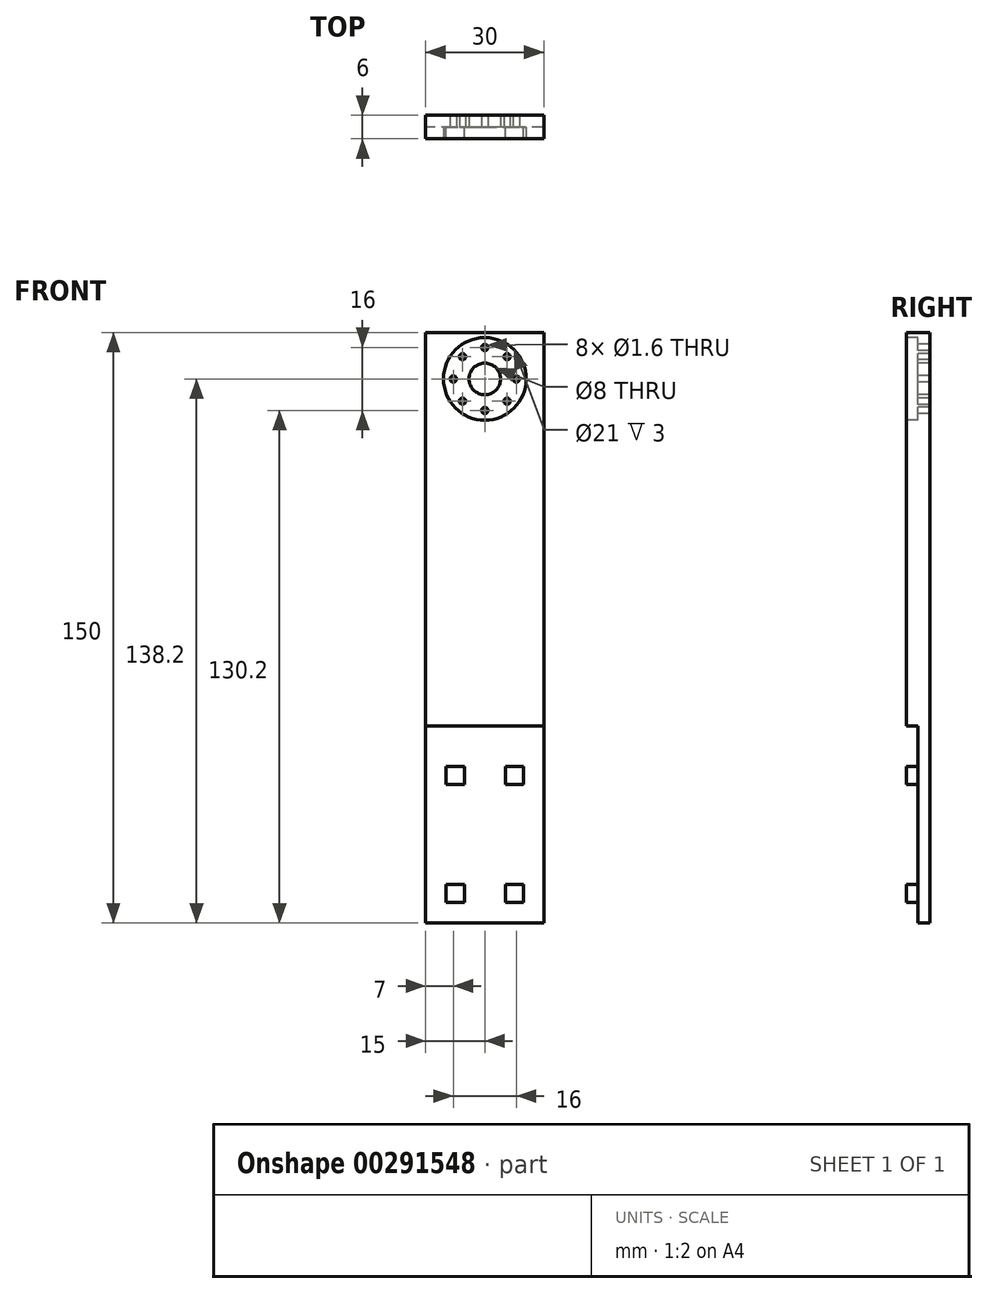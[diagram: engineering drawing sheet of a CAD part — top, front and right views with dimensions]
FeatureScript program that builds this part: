
annotation { "Feature Type Name" : "Feature", "Feature Type Description" : "" }
export const myFeature = defineFeature(function(context is Context, id is Id, definition is map)
    precondition{}
    {
        {
            var Q0;
            Q0=qCreatedBy(makeId("Top.planeOp"),FACE);
            var sketch = newSketch(context, id + "F0", { "sketchPlane" : qUnion([Q0])});
            skLineSegment(sketch, "E0.bottom", {"start": v(-15, 3) * mm, "end": v(15, 3) * mm});
            skLineSegment(sketch, "E0.top", {"start": v(-15, -3) * mm, "end": v(15, -3) * mm});
            skLineSegment(sketch, "E0.left", {"start": v(-15, 3) * mm, "end": v(-15, -3) * mm});
            skLineSegment(sketch, "E0.right", {"start": v(15, 3) * mm, "end": v(15, -3) * mm});
            skSolve(sketch);
        }
        {
            var Q0;
            Q0=qSketchRegion(id+"F0",true);
            extrude(context, id + "F1", {"entities" : qUnion([Q0]), "depth" : 150 * mm, "offsetDistance" : 25 * mm});
        }
        {
            var Q0;
            Q0=makeQuery(id+"F1.opExtrude","SWEPT_FACE",FACE,{"disambiguationData":[OSD([sQuery(id+"F0.wireOp",EDGE,"E0.top")])]});
            var sketch = newSketch(context, id + "F2", { "sketchPlane" : qUnion([Q0])});
            skCircle(sketch, "E1", {"center": v(0, 146.2) * mm, "radius": 0.8 * mm});
            skCircle(sketch, "E2", {"center": v(0, 138.2) * mm, "radius": 4 * mm});
            skCircle(sketch, "E3.1.0", {"center": v(-5.66, 143.86) * mm, "radius": 0.8 * mm});
            skCircle(sketch, "E3.2.0", {"center": v(-8, 138.2) * mm, "radius": 0.8 * mm});
            skCircle(sketch, "E3.3.0", {"center": v(-5.66, 132.54) * mm, "radius": 0.8 * mm});
            skCircle(sketch, "E3.4.0", {"center": v(0, 130.2) * mm, "radius": 0.8 * mm});
            skCircle(sketch, "E3.5.0", {"center": v(5.66, 132.54) * mm, "radius": 0.8 * mm});
            skCircle(sketch, "E3.6.0", {"center": v(8, 138.2) * mm, "radius": 0.8 * mm});
            skCircle(sketch, "E3.7.0", {"center": v(5.66, 143.86) * mm, "radius": 0.8 * mm});
            skSolve(sketch);
        }
        {
            var Q0;
            Q0=qSketchRegion(id+"F2",true);
            extrude(context, id + "F3", {"entities" : qUnion([Q0]), "operationType" : NewBodyOperationType.REMOVE, "endBound" : BoundingType.UP_TO_NEXT, "oppositeDirection" : true, "depth" : 25 * mm});
        }
        {
            var Q0;
            Q0=makeQuery(id+"F1.opExtrude","SWEPT_FACE",FACE,{"disambiguationData":[OSD([sQuery(id+"F0.wireOp",EDGE,"E0.left")])]});
            var sketch = newSketch(context, id + "F4", { "sketchPlane" : qUnion([Q0])});
            skLineSegment(sketch, "E4.bottom", {"start": v(0, 50) * mm, "end": v(3, 50) * mm});
            skLineSegment(sketch, "E4.top", {"start": v(0, 0) * mm, "end": v(3, 0) * mm});
            skLineSegment(sketch, "E4.left", {"start": v(0, 50) * mm, "end": v(0, 0) * mm});
            skLineSegment(sketch, "E4.right", {"start": v(3, 50) * mm, "end": v(3, 0) * mm});
            skSolve(sketch);
        }
        {
            var Q0;
            Q0=makeQuery(id+"F4.imprint","IMPRINT",FACE,{"disambiguationData":[TD([[makeQuery(id+"F4.imprint","IMPRINT",EDGE,{"derivedFrom":sQuery(id+"F4.wireOp",EDGE,"E4.bottom")}),-1.0]])]});
            extrude(context, id + "F5", {"entities" : qUnion([Q0]), "operationType" : NewBodyOperationType.REMOVE, "endBound" : BoundingType.UP_TO_NEXT, "oppositeDirection" : true, "depth" : 25 * mm, "offsetDistance" : 25 * mm});
        }
        {
            var Q0;
            Q0=makeQuery(id+"F5.boolean.opBoolean","COPY",FACE,{"derivedFrom":makeQuery(id+"F5.opExtrude","SWEPT_FACE",FACE,{"disambiguationData":[OSD([sQuery(id+"F4.wireOp",EDGE,"E4.left")])]})});
            var sketch = newSketch(context, id + "F6", { "sketchPlane" : qUnion([Q0])});
            skLineSegment(sketch, "E5.0", {"start": v(-9.8, 39.8) * mm, "end": v(-5.2, 39.8) * mm});
            skLineSegment(sketch, "E5.1", {"start": v(-9.8, 39.8) * mm, "end": v(-9.8, 35.2) * mm});
            skLineSegment(sketch, "E5.2", {"start": v(-9.8, 35.2) * mm, "end": v(-5.2, 35.2) * mm});
            skLineSegment(sketch, "E5.3", {"start": v(-5.2, 39.8) * mm, "end": v(-5.2, 35.2) * mm});
            skLineSegment(sketch, "E6.0", {"start": v(-9.8, 9.8) * mm, "end": v(-5.2, 9.8) * mm});
            skLineSegment(sketch, "E6.1", {"start": v(-9.8, 5.2) * mm, "end": v(-9.8, 9.8) * mm});
            skLineSegment(sketch, "E6.2", {"start": v(-9.8, 5.2) * mm, "end": v(-5.2, 5.2) * mm});
            skLineSegment(sketch, "E6.3", {"start": v(-5.2, 5.2) * mm, "end": v(-5.2, 9.8) * mm});
            skLineSegment(sketch, "E7.0", {"start": v(5.2, 5.2) * mm, "end": v(5.2, 9.8) * mm});
            skLineSegment(sketch, "E7.1", {"start": v(9.8, 5.2) * mm, "end": v(5.2, 5.2) * mm});
            skLineSegment(sketch, "E7.2", {"start": v(9.8, 5.2) * mm, "end": v(9.8, 9.8) * mm});
            skLineSegment(sketch, "E7.3", {"start": v(9.8, 9.8) * mm, "end": v(5.2, 9.8) * mm});
            skLineSegment(sketch, "E8.0", {"start": v(9.8, 39.8) * mm, "end": v(5.2, 39.8) * mm});
            skLineSegment(sketch, "E8.1", {"start": v(9.8, 39.8) * mm, "end": v(9.8, 35.2) * mm});
            skLineSegment(sketch, "E8.2", {"start": v(9.8, 35.2) * mm, "end": v(5.2, 35.2) * mm});
            skLineSegment(sketch, "E8.3", {"start": v(5.2, 39.8) * mm, "end": v(5.2, 35.2) * mm});
            skSolve(sketch);
        }
        {
            var Q0;
            Q0=makeQuery(id+"F6.imprint","IMPRINT",FACE,{"disambiguationData":[TD([[makeQuery(id+"F6.imprint","IMPRINT",EDGE,{"derivedFrom":sQuery(id+"F6.wireOp",EDGE,"E8.0")}),1.0]])]});
            var Q1;
            Q1=makeQuery(id+"F6.imprint","IMPRINT",FACE,{"disambiguationData":[TD([[makeQuery(id+"F6.imprint","IMPRINT",EDGE,{"derivedFrom":sQuery(id+"F6.wireOp",EDGE,"E5.0")}),-1.0]])]});
            var Q2;
            Q2=makeQuery(id+"F6.imprint","IMPRINT",FACE,{"disambiguationData":[TD([[makeQuery(id+"F6.imprint","IMPRINT",EDGE,{"derivedFrom":sQuery(id+"F6.wireOp",EDGE,"E6.0")}),-1.0]])]});
            var Q3;
            Q3=makeQuery(id+"F6.imprint","IMPRINT",FACE,{"disambiguationData":[TD([[makeQuery(id+"F6.imprint","IMPRINT",EDGE,{"derivedFrom":sQuery(id+"F6.wireOp",EDGE,"E7.0")}),-1.0]])]});
            extrude(context, id + "F7", {"entities" : qUnion([Q0, Q1, Q2, Q3]), "operationType" : NewBodyOperationType.ADD, "depth" : 3 * mm, "offsetDistance" : 25 * mm});
        }
        {
            var Q0;
            Q0=makeQuery(id+"F1.opExtrude","SWEPT_FACE",FACE,{"disambiguationData":[OSD([sQuery(id+"F0.wireOp",EDGE,"E0.top")])]});
            var sketch = newSketch(context, id + "F8", { "sketchPlane" : qUnion([Q0])});
            skCircle(sketch, "E9", {"center": v(0, 138.2) * mm, "radius": 10.5 * mm});
            skSolve(sketch);
        }
        {
            var Q0;
            Q0 = qSketchRegion(id + "F8", true);
            extrude(context, id + "F9", {"entities" : qUnion([Q0]), "operationType" : NewBodyOperationType.REMOVE, "oppositeDirection" : true, "depth" : 3 * mm, "offsetDistance" : 25 * mm});
        }
    });
